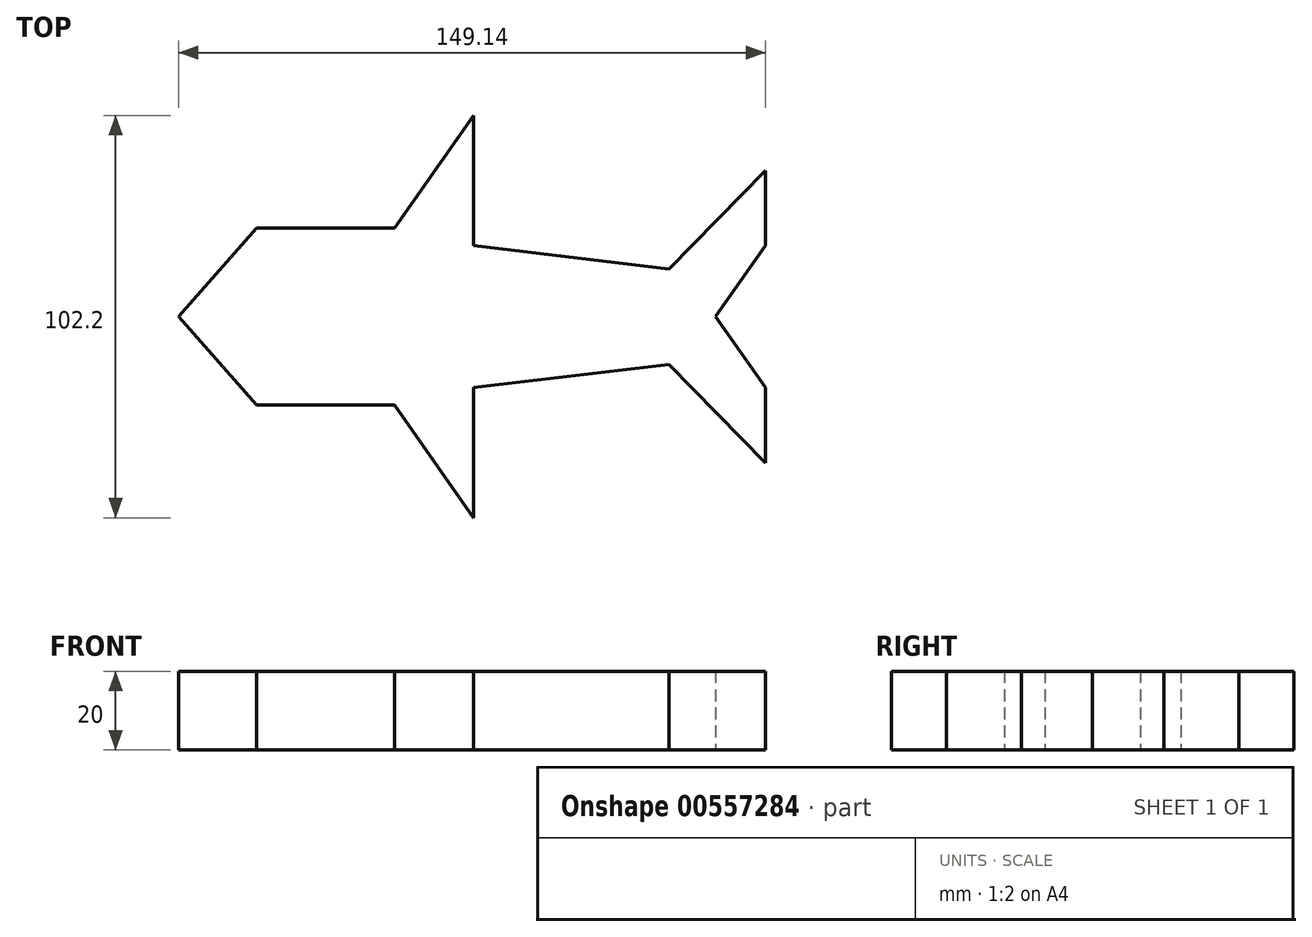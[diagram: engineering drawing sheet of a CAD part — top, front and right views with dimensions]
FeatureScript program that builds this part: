
annotation { "Feature Type Name" : "Feature", "Feature Type Description" : "" }
export const myFeature = defineFeature(function(context is Context, id is Id, definition is map)
    precondition{}
    {
        {
            var Q0;
            Q0=qCreatedBy(makeId("Top.planeOp"),FACE);
            var sketch = newSketch(context, id + "F0", { "sketchPlane" : qUnion([Q0])});
            skLineSegment(sketch, "E0", {"start": v(0, 0) * mm, "end": v(-75, 0) * mm, "construction": true});
            skLineSegment(sketch, "E1", {"start": v(-75, 0) * mm, "end": v(-55.1, 22.45) * mm});
            skLineSegment(sketch, "E2", {"start": v(-55.1, 22.45) * mm, "end": v(-20.1, 22.45) * mm});
            skLineSegment(sketch, "E3", {"start": v(-20.1, 22.45) * mm, "end": v(0, 51.1) * mm});
            skLineSegment(sketch, "E4", {"start": v(0, 51.1) * mm, "end": v(0, 18.06) * mm});
            skLineSegment(sketch, "E5", {"start": v(0, 18.06) * mm, "end": v(49.65, 12.11) * mm});
            skLineSegment(sketch, "E6", {"start": v(49.65, 12.11) * mm, "end": v(74.14, 37.12) * mm});
            skLineSegment(sketch, "E7", {"start": v(74.14, 37.12) * mm, "end": v(74.14, 18.06) * mm});
            skLineSegment(sketch, "E8", {"start": v(74.14, 18.06) * mm, "end": v(61.46, 0) * mm});
            skLineSegment(sketch, "E9", {"start": v(0, 0) * mm, "end": v(61.46, 0) * mm, "construction": true});
            skLineSegment(sketch, "E10.MirrorCS", {"start": v(-75, 0) * mm, "end": v(-55.1, -22.45) * mm});
            skLineSegment(sketch, "E11.MirrorCS", {"start": v(-55.1, -22.45) * mm, "end": v(-20.1, -22.45) * mm});
            skLineSegment(sketch, "E12.MirrorCS", {"start": v(-20.1, -22.45) * mm, "end": v(0, -51.1) * mm});
            skLineSegment(sketch, "E13.MirrorCS", {"start": v(74.14, -37.12) * mm, "end": v(74.14, -18.06) * mm});
            skLineSegment(sketch, "E14.MirrorCS", {"start": v(49.65, -12.11) * mm, "end": v(74.14, -37.12) * mm});
            skLineSegment(sketch, "E15.MirrorCS", {"start": v(74.14, -18.06) * mm, "end": v(61.46, 0) * mm});
            skLineSegment(sketch, "E16.MirrorCS", {"start": v(0, -51.1) * mm, "end": v(0, -18.06) * mm});
            skLineSegment(sketch, "E17.MirrorCS", {"start": v(0, -18.06) * mm, "end": v(49.65, -12.11) * mm});
            skSolve(sketch);
        }
        {
            var Q0;
            Q0=makeQuery(id+"F0.imprint","IMPRINT",FACE,{"disambiguationData":[TD([[makeQuery(id+"F0.imprint","IMPRINT",EDGE,{"derivedFrom":sQuery(id+"F0.wireOp",EDGE,"E1")}),-1.0]])]});
            extrude(context, id + "F1", {"entities" : qUnion([Q0]), "endBound" : BoundingType.SYMMETRIC, "depth" : 20 * mm, "offsetDistance" : 25 * mm});
        }
    });
